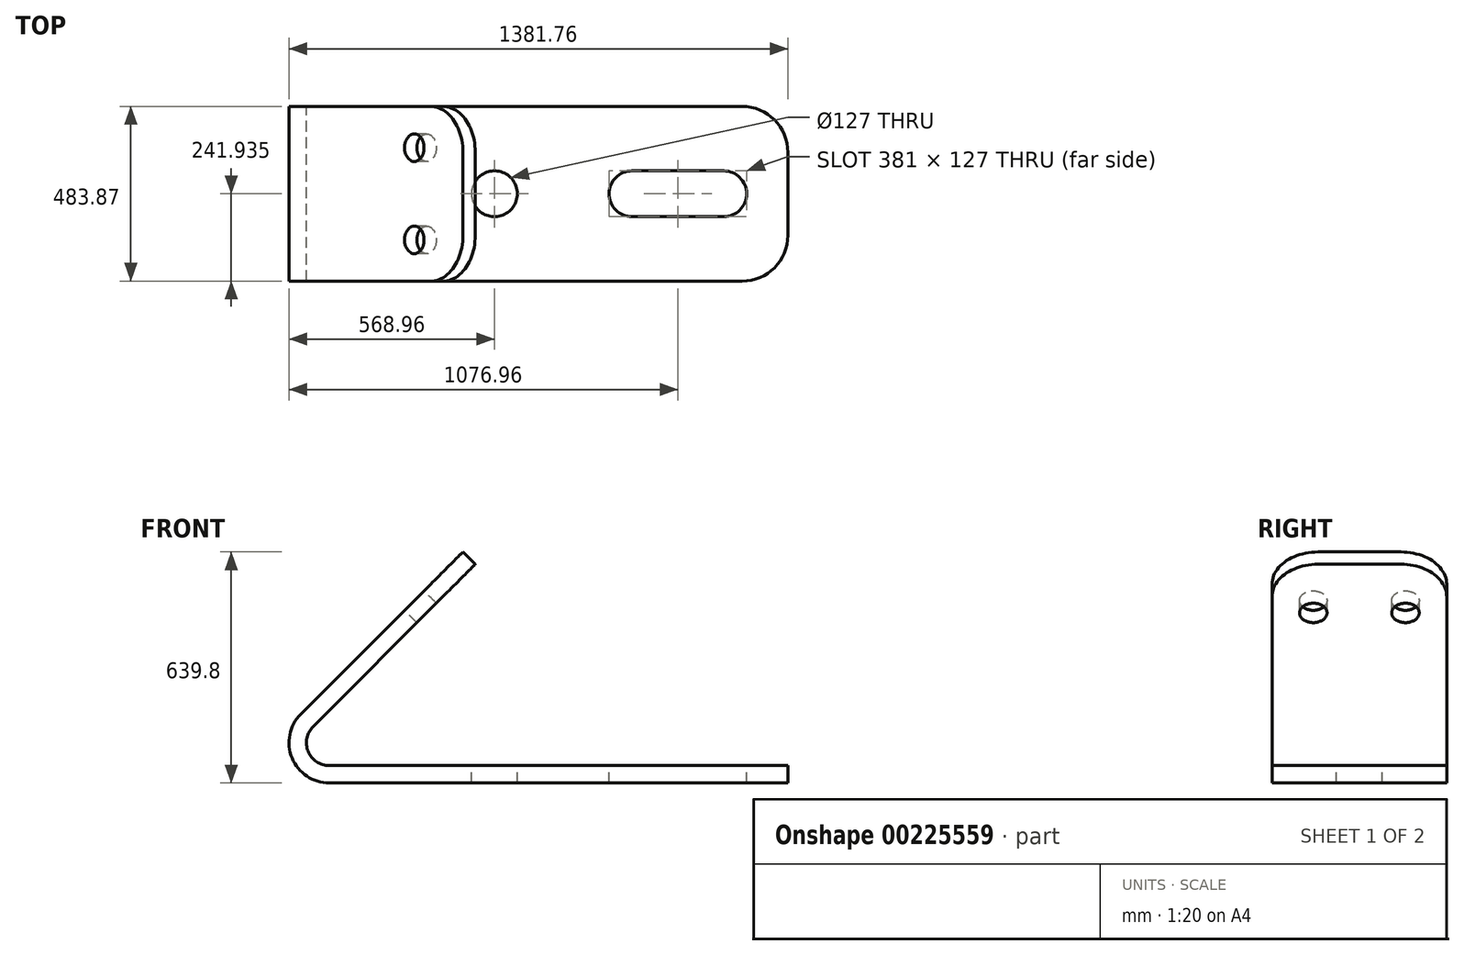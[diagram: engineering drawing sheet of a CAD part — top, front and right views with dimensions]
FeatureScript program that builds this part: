
annotation { "Feature Type Name" : "Feature", "Feature Type Description" : "" }
export const myFeature = defineFeature(function(context is Context, id is Id, definition is map)
    precondition{}
    {
        {
            var Q0;
            Q0=qCreatedBy(makeId("Front.planeOp"),FACE);
            var sketch = newSketch(context, id + "F0", { "sketchPlane" : qUnion([Q0])});
            skLineSegment(sketch, "E0", {"start": v(0, 0) * mm, "end": v(1270, 0) * mm});
            skLineSegment(sketch, "E1", {"start": v(1270, 0) * mm, "end": v(1270, 48.26) * mm});
            skLineSegment(sketch, "E2", {"start": v(1270, 48.26) * mm, "end": v(0, 48.26) * mm});
            skLineSegment(sketch, "E3", {"start": v(0, 0) * mm, "end": v(0, 111.76) * mm, "construction": true});
            skArc(sketch, "E4", {"start": v(-79.03, 190.79) * mm, "mid": v(-103.25, 69) * mm, "end": v(0, 0) * mm});
            skLineSegment(sketch, "E5", {"start": v(-79.03, 190.79) * mm, "end": v(369.99, 639.8) * mm});
            skLineSegment(sketch, "E6", {"start": v(369.99, 639.8) * mm, "end": v(404.11, 605.67) * mm});
            skArc(sketch, "E7", {"start": v(-44.9, 156.66) * mm, "mid": v(-58.67, 87.46) * mm, "end": v(0, 48.26) * mm});
            skLineSegment(sketch, "E8", {"start": v(404.11, 605.67) * mm, "end": v(-44.9, 156.66) * mm});
            skSolve(sketch);
        }
        {
            var Q0;
            Q0 = qSketchRegion(id + "F0", true);
            extrude(context, id + "F1", {"entities" : qUnion([Q0]), "depth" : 483.87 * mm});
        }
        {
            var Q0;
            Q0=makeQuery(id+"F1.opExtrude","SWEPT_FACE",FACE,{"disambiguationData":[OSD([sQuery(id+"F0.wireOp",EDGE,"E5")])]});
            var sketch = newSketch(context, id + "F2", { "sketchPlane" : qUnion([Q0])});
            skCircle(sketch, "E9", {"center": v(114.3, 523.53) * mm, "radius": 38.1 * mm});
            skCircle(sketch, "E10", {"center": v(369.57, 523.53) * mm, "radius": 38.1 * mm});
            skSolve(sketch);
        }
        {
            var Q0;
            Q0 = qSketchRegion(id + "F2", true);
            var Q1;
            Q1=makeQuery(id+"F1.opExtrude","SWEPT_FACE",FACE,{"disambiguationData":[OSD([sQuery(id+"F0.wireOp",EDGE,"E8")])]});
            extrude(context, id + "F3", {"entities" : qUnion([Q0]), "operationType" : NewBodyOperationType.REMOVE, "endBound" : BoundingType.UP_TO_SURFACE, "oppositeDirection" : true, "endBoundEntityFace" : qUnion([Q1]), "depth" : 25.4 * mm});
        }
        {
            var Q0;
            Q0=makeQuery(id+"F1.opExtrude","CAP_EDGE",EDGE,{"disambiguationData":[OSD([sQuery(id+"F0.wireOp",EDGE,"E6")])],"isStart":true});
            var Q1;
            Q1=makeQuery(id+"F1.opExtrude","CAP_EDGE",EDGE,{"disambiguationData":[OSD([sQuery(id+"F0.wireOp",EDGE,"E6")])],"isStart":false});
            fillet(context, id + "F4", {"entities" : qUnion([Q0, Q1]), "radius" : 127 * mm, "tangentPropagation" : true, "allowEdgeOverflow" : false});
        }
        {
            var Q0;
            Q0=makeQuery(id+"F1.opExtrude","SWEPT_FACE",FACE,{"disambiguationData":[OSD([sQuery(id+"F0.wireOp",EDGE,"E2")])]});
            var sketch = newSketch(context, id + "F5", { "sketchPlane" : qUnion([Q0])});
            skLineSegment(sketch, "E11", {"start": v(457.2, -241.94) * mm, "end": v(1270, -241.94) * mm, "construction": true});
            skCircle(sketch, "E12", {"center": v(457.2, -241.94) * mm, "radius": 63.5 * mm});
            skArc(sketch, "E13", {"start": v(1092.2, -305.44) * mm, "mid": v(1155.7, -241.94) * mm, "end": v(1092.2, -178.44) * mm});
            skLineSegment(sketch, "E14", {"start": v(1092.2, -178.44) * mm, "end": v(965.2, -178.44) * mm});
            skLineSegment(sketch, "E15", {"start": v(1092.2, -305.44) * mm, "end": v(965.2, -305.44) * mm});
            skLineSegment(sketch, "E16", {"start": v(965.2, -305.44) * mm, "end": v(965.2, -77.54) * mm, "construction": true});
            skLineSegment(sketch, "E17.MirrorCS", {"start": v(838.2, -178.44) * mm, "end": v(965.2, -178.44) * mm});
            skArc(sketch, "E18.MirrorCS", {"start": v(838.2, -305.44) * mm, "mid": v(774.7, -241.94) * mm, "end": v(838.2, -178.44) * mm});
            skLineSegment(sketch, "E19.MirrorCS", {"start": v(838.2, -305.44) * mm, "end": v(965.2, -305.44) * mm});
            skSolve(sketch);
        }
        {
            var Q0;
            Q0 = qSketchRegion(id + "F5", true);
            extrude(context, id + "F6", {"entities" : qUnion([Q0]), "operationType" : NewBodyOperationType.REMOVE, "endBound" : BoundingType.THROUGH_ALL, "oppositeDirection" : true, "depth" : 25.4 * mm});
        }
        {
            var Q0;
            Q0=makeQuery(id+"F1.opExtrude","CAP_EDGE",EDGE,{"disambiguationData":[OSD([sQuery(id+"F0.wireOp",EDGE,"E1")])],"isStart":false});
            var Q1;
            Q1=makeQuery(id+"F1.opExtrude","CAP_EDGE",EDGE,{"disambiguationData":[OSD([sQuery(id+"F0.wireOp",EDGE,"E1")])],"isStart":true});
            fillet(context, id + "F7", {"entities" : qUnion([Q0, Q1]), "radius" : 127 * mm, "tangentPropagation" : true, "allowEdgeOverflow" : false});
        }
    });
